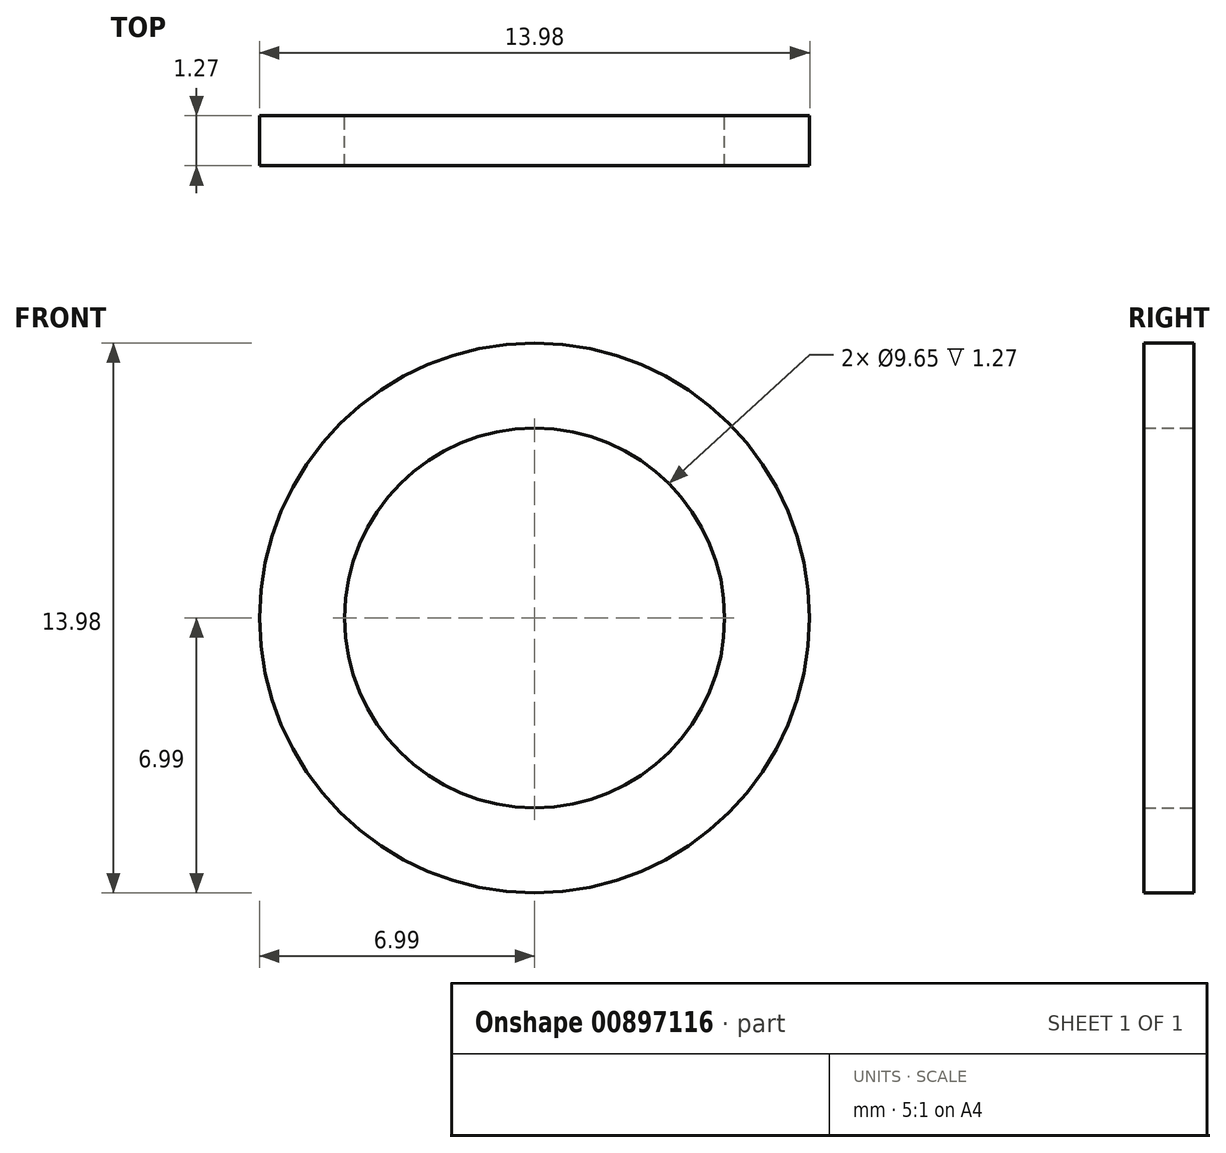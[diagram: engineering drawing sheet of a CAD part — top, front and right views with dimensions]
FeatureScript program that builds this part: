
annotation { "Feature Type Name" : "Feature", "Feature Type Description" : "" }
export const myFeature = defineFeature(function(context is Context, id is Id, definition is map)
    precondition{}
    {
        {
            var Q0;
            Q0=qCreatedBy(makeId("Front.planeOp"),FACE);
            var sketch = newSketch(context, id + "F0", { "sketchPlane" : qUnion([Q0])});
            skCircle(sketch, "E0", {"center": v(0, 0) * mm, "radius": 4.83 * mm});
            skCircle(sketch, "E1", {"center": v(0, 0) * mm, "radius": 6.99 * mm});
            skSolve(sketch);
        }
        {
            var Q0;
            Q0=qSketchRegion(id+"F0",true);
            extrude(context, id + "F1", {"entities" : qUnion([Q0]), "depth" : 1.27 * mm});
        }
    });
